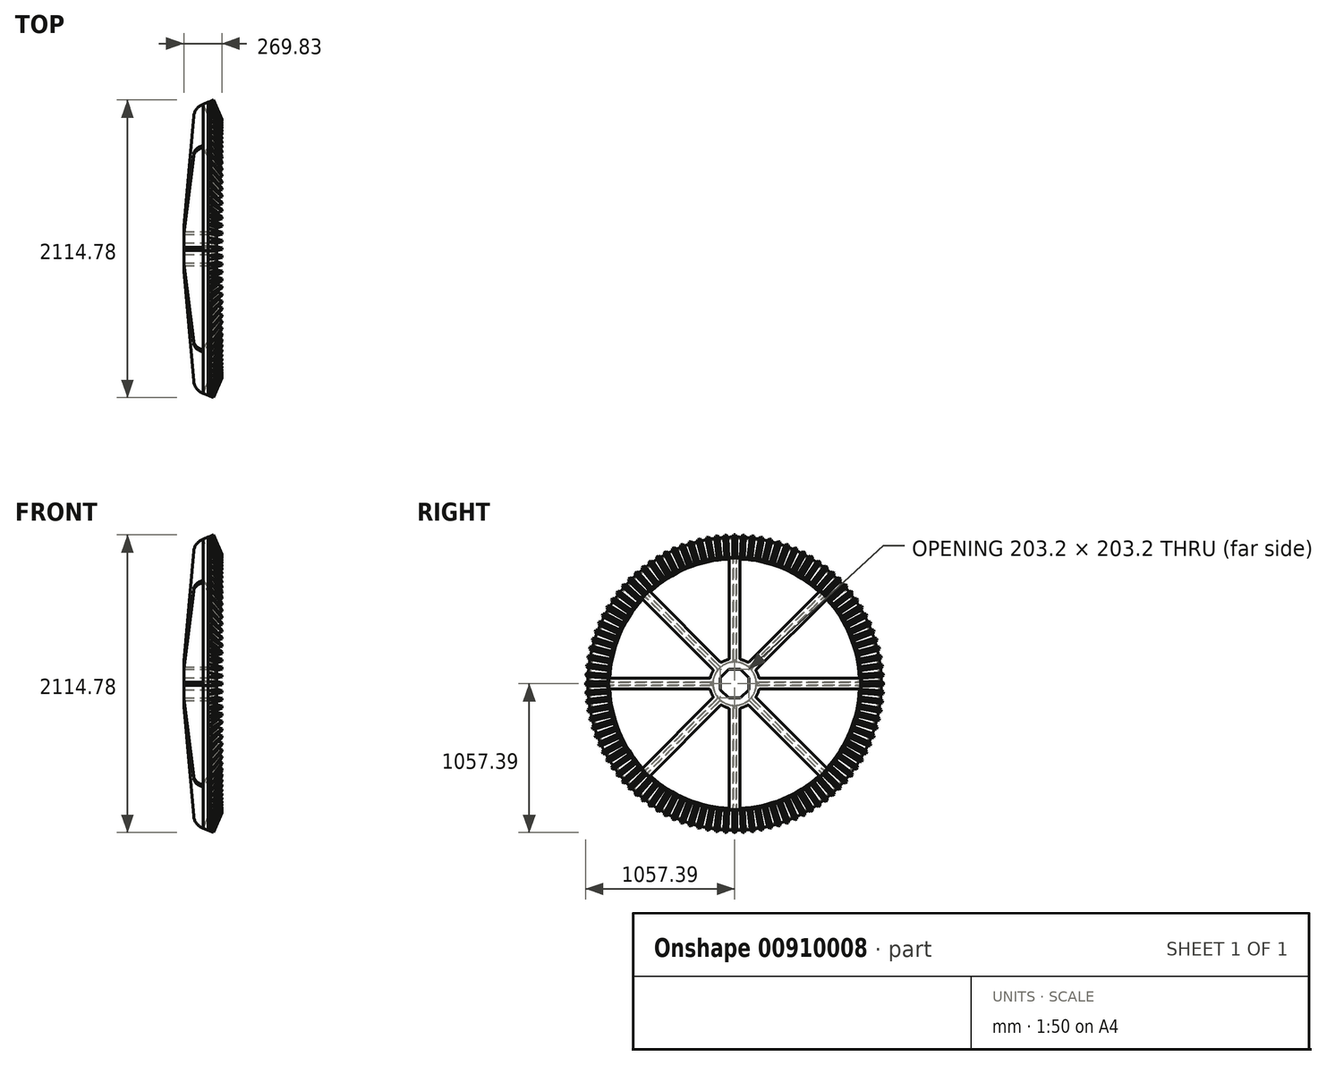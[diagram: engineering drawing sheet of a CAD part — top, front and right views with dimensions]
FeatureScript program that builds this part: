
annotation { "Feature Type Name" : "Feature", "Feature Type Description" : "" }
export const myFeature = defineFeature(function(context is Context, id is Id, definition is map)
    precondition{}
    {
        {
            var Q0;
            Q0=qCreatedBy(makeId("Front.planeOp"),FACE);
            var sketch = newSketch(context, id + "F0", { "sketchPlane" : qUnion([Q0])});
            skLineSegment(sketch, "E0.bottom", {"start": v(0, 0) * mm, "end": v(-215.9, 0) * mm});
            skLineSegment(sketch, "E0.top", {"start": v(-19.05, 154.2) * mm, "end": v(-215.9, 154.2) * mm});
            skLineSegment(sketch, "E0.right", {"start": v(-215.9, 0) * mm, "end": v(-215.9, 154.2) * mm});
            skLineSegment(sketch, "E1", {"start": v(-43.01, 1041.4) * mm, "end": v(16.07, 900.92) * mm});
            skLineSegment(sketch, "E2", {"start": v(16.07, 900.92) * mm, "end": v(-19.05, 886.15) * mm});
            skLineSegment(sketch, "E3", {"start": v(-19.05, 886.15) * mm, "end": v(-78.13, 1026.63) * mm});
            skLineSegment(sketch, "E4", {"start": v(-78.13, 1026.63) * mm, "end": v(-43.01, 1041.4) * mm});
            skLineSegment(sketch, "E5", {"start": v(-19.05, 154.2) * mm, "end": v(-19.05, 177.8) * mm});
            skLineSegment(sketch, "E6", {"start": v(-19.05, 177.8) * mm, "end": v(0, 177.8) * mm});
            skLineSegment(sketch, "E7", {"start": v(0, 177.8) * mm, "end": v(0, 0) * mm});
            skLineSegment(sketch, "E8", {"start": v(-13.47, 971.16) * mm, "end": v(-48.6, 956.39) * mm, "construction": true});
            skLineSegment(sketch, "E9", {"start": v(0, 0) * mm, "end": v(215.9, 0) * mm, "construction": true});
            skSolve(sketch);
        }
        {
            var Q0;
            Q0=makeQuery(id+"F0.imprint","IMPRINT",FACE,{"disambiguationData":[TD([[makeQuery(id+"F0.imprint","IMPRINT",EDGE,{"derivedFrom":sQuery(id+"F0.wireOp",EDGE,"E0.bottom")}),-1.0]])]});
            var Q1;
            Q1=sQuery(id+"F0.wireOp",EDGE,"E0.bottom");
            revolve(context, id + "F1", {"surfaceOperationType" : NewSurfaceOperationType.NEW, "entities" : qUnion([Q0]), "axis" : qUnion([Q1]), "revolveType" : RevolveType.SYMMETRIC, "angle" : 45 * degree});
        }
        {
            var Q0;
            Q0=qCreatedBy(makeId("Front.planeOp"),FACE);
            var sketch = newSketch(context, id + "F2", { "sketchPlane" : qUnion([Q0])});
            skLineSegment(sketch, "E10.bottom", {"start": v(0, 154.2) * mm, "end": v(-19.05, 154.2) * mm});
            skLineSegment(sketch, "E10.top", {"start": v(0, 894.16) * mm, "end": v(-19.05, 886.15) * mm});
            skLineSegment(sketch, "E10.left", {"start": v(0, 154.2) * mm, "end": v(0, 894.16) * mm});
            skLineSegment(sketch, "E10.right", {"start": v(-19.05, 154.2) * mm, "end": v(-19.05, 886.15) * mm});
            skLineSegment(sketch, "E11", {"start": v(-19.05, 886.15) * mm, "end": v(-78.13, 1026.63) * mm});
            skLineSegment(sketch, "E12", {"start": v(-78.13, 1026.63) * mm, "end": v(-83.99, 1024.17) * mm});
            skLineSegment(sketch, "E13", {"start": v(-145.8, 939.53) * mm, "end": v(-215.9, 152.4) * mm});
            skLineSegment(sketch, "E14", {"start": v(-215.9, 0) * mm, "end": v(-19.05, 0) * mm});
            skLineSegment(sketch, "E15", {"start": v(-19.05, 0) * mm, "end": v(-19.05, 154.2) * mm});
            skPoint(sketch, "E16.visualSharp", {"position": v(-140.37, 1000.45) * mm});
            skArc(sketch, "E16.filletArc", {"start": v(-83.99, 1024.17) * mm, "mid": v(-126.65, 990.43) * mm, "end": v(-145.8, 939.53) * mm});
            skLineSegment(sketch, "E17", {"start": v(-215.9, 152.4) * mm, "end": v(-215.9, 0) * mm});
            skSolve(sketch);
        }
        {
            var Q0;
            Q0=makeQuery(id+"F2.imprint","IMPRINT",FACE,{"disambiguationData":[TD([[makeQuery(id+"F2.imprint","IMPRINT",EDGE,{"derivedFrom":sQuery(id+"F2.wireOp",EDGE,"E10.bottom")}),-1.0]])]});
            extrude(context, id + "F3", {"entities" : qUnion([Q0]), "operationType" : NewBodyOperationType.ADD, "depth" : 76.2 * mm, "offsetDistance" : 25 * mm, "symmetric" : true});
        }
        {
            var Q0;
            Q0=makeQuery(id+"F2.imprint","IMPRINT",FACE,{"disambiguationData":[TD([[makeQuery(id+"F2.imprint","IMPRINT",EDGE,{"derivedFrom":sQuery(id+"F2.wireOp",EDGE,"E10.right")}),1.0]])]});
            extrude(context, id + "F4", {"entities" : qUnion([Q0]), "operationType" : NewBodyOperationType.ADD, "depth" : 22.23 * mm, "offsetDistance" : 25 * mm, "symmetric" : true});
        }
        {
            var Q0;
            Q0=makeQuery(id+"F0.imprint","IMPRINT",FACE,{"disambiguationData":[TD([[makeQuery(id+"F0.imprint","IMPRINT",EDGE,{"derivedFrom":sQuery(id+"F0.wireOp",EDGE,"E1")}),-1.0]])]});
            var Q1;
            Q1=sQuery(id+"F0.wireOp",EDGE,"E0.bottom");
            revolve(context, id + "F5", {"operationType" : NewBodyOperationType.ADD, "surfaceOperationType" : NewSurfaceOperationType.NEW, "entities" : qUnion([Q0]), "axis" : qUnion([Q1]), "revolveType" : RevolveType.SYMMETRIC, "angle" : 45 * degree});
        }
        {
            var Q0;
            Q0=makeQuery(id+"F4.boolean.opBoolean","INTERSECT",EDGE,{"derivedFrom":[makeQuery(id+"F1.opRevolve","SWEPT_FACE",FACE,{"disambiguationData":[OSD([sQuery(id+"F0.wireOp",EDGE,"E0.top")])]}),makeQuery(id+"F4.opExtrude","CAP_FACE",FACE,{"disambiguationData":[OSD([sQuery(id+"F2.wireOp",EDGE,"E10.right"),sQuery(id+"F2.wireOp",EDGE,"E11"),sQuery(id+"F2.wireOp",EDGE,"E12"),sQuery(id+"F2.wireOp",EDGE,"PsCl8xdc-vel7-nRXP-WIJk-A4uk1FeWP0Ge"),sQuery(id+"F2.wireOp",EDGE,"E13"),sQuery(id+"F2.wireOp",EDGE,"E14"),sQuery(id+"F2.wireOp",EDGE,"E15")])],"isStart":false})]});
            var Q1;
            {var subQ0=sQuery(id+"F0.wireOp",EDGE,"E5");var subQ2=sQuery(id+"F0.wireOp",EDGE,"E0.top");Q1=makeQuery(id+"F4.boolean.opBoolean","SPLIT",EDGE,{"disambiguationData":[TD([makeQuery(id+"F1.opRevolve","CAP_FACE",FACE,{"disambiguationData":[OSD([sQuery(id+"F0.wireOp",EDGE,"E0.bottom"),subQ2,sQuery(id+"F0.wireOp",EDGE,"E0.right"),subQ0,sQuery(id+"F0.wireOp",EDGE,"E6"),sQuery(id+"F0.wireOp",EDGE,"E7")])],"isStart":false})])],"derivedFrom":makeQuery(id+"F1.opRevolve","SWEPT_EDGE",EDGE,{"disambiguationData":[OSD([subQ2,subQ0])]})});}
            var Q2;
            Q2=makeQuery(id+"F4.opExtrude","CAP_EDGE",EDGE,{"disambiguationData":[OSD([sQuery(id+"F2.wireOp",EDGE,"E10.right"),sQuery(id+"F2.wireOp",EDGE,"E15")])],"isStart":false});
            var Q3;
            Q3=makeQuery(id+"F3.boolean.opBoolean","INTERSECT",EDGE,{"derivedFrom":[makeQuery(id+"F1.opRevolve","SWEPT_FACE",FACE,{"disambiguationData":[OSD([sQuery(id+"F0.wireOp",EDGE,"E6")])]}),makeQuery(id+"F3.opExtrude","CAP_FACE",FACE,{"disambiguationData":[OSD([sQuery(id+"F2.wireOp",EDGE,"E10.bottom"),sQuery(id+"F2.wireOp",EDGE,"E10.top"),sQuery(id+"F2.wireOp",EDGE,"E10.left"),sQuery(id+"F2.wireOp",EDGE,"E10.right")])],"isStart":false})]});
            var Q4;
            Q4=makeQuery(id+"F4.boolean.opBoolean","INTERSECT",EDGE,{"derivedFrom":[makeQuery(id+"F1.opRevolve","SWEPT_FACE",FACE,{"disambiguationData":[OSD([sQuery(id+"F0.wireOp",EDGE,"E0.top")])]}),makeQuery(id+"F4.opExtrude","CAP_FACE",FACE,{"disambiguationData":[OSD([sQuery(id+"F2.wireOp",EDGE,"E10.right"),sQuery(id+"F2.wireOp",EDGE,"E11"),sQuery(id+"F2.wireOp",EDGE,"E12"),sQuery(id+"F2.wireOp",EDGE,"PsCl8xdc-vel7-nRXP-WIJk-A4uk1FeWP0Ge"),sQuery(id+"F2.wireOp",EDGE,"E13"),sQuery(id+"F2.wireOp",EDGE,"E14"),sQuery(id+"F2.wireOp",EDGE,"E15")])],"isStart":true})]});
            var Q5;
            {var subQ0=sQuery(id+"F0.wireOp",EDGE,"E5");var subQ2=sQuery(id+"F0.wireOp",EDGE,"E0.top");Q5=makeQuery(id+"F4.boolean.opBoolean","SPLIT",EDGE,{"disambiguationData":[TD([makeQuery(id+"F1.opRevolve","CAP_FACE",FACE,{"disambiguationData":[OSD([sQuery(id+"F0.wireOp",EDGE,"E0.bottom"),subQ2,sQuery(id+"F0.wireOp",EDGE,"E0.right"),subQ0,sQuery(id+"F0.wireOp",EDGE,"E6"),sQuery(id+"F0.wireOp",EDGE,"E7")])],"isStart":true})])],"derivedFrom":makeQuery(id+"F1.opRevolve","SWEPT_EDGE",EDGE,{"disambiguationData":[OSD([subQ2,subQ0])]})});}
            var Q6;
            Q6=makeQuery(id+"F4.opExtrude","CAP_EDGE",EDGE,{"disambiguationData":[OSD([sQuery(id+"F2.wireOp",EDGE,"E10.right"),sQuery(id+"F2.wireOp",EDGE,"E15")])],"isStart":true});
            var Q7;
            Q7=makeQuery(id+"F3.boolean.opBoolean","INTERSECT",EDGE,{"derivedFrom":[makeQuery(id+"F1.opRevolve","SWEPT_FACE",FACE,{"disambiguationData":[OSD([sQuery(id+"F0.wireOp",EDGE,"E6")])]}),makeQuery(id+"F3.opExtrude","CAP_FACE",FACE,{"disambiguationData":[OSD([sQuery(id+"F2.wireOp",EDGE,"E10.bottom"),sQuery(id+"F2.wireOp",EDGE,"E10.top"),sQuery(id+"F2.wireOp",EDGE,"E10.left"),sQuery(id+"F2.wireOp",EDGE,"E10.right")])],"isStart":true})]});
            var Q8;
            Q8=makeQuery(id+"F5.boolean.opBoolean","INTERSECT",EDGE,{"derivedFrom":[makeQuery(id+"F4.opExtrude","CAP_FACE",FACE,{"disambiguationData":[OSD([sQuery(id+"F2.wireOp",EDGE,"E10.right"),sQuery(id+"F2.wireOp",EDGE,"E11"),sQuery(id+"F2.wireOp",EDGE,"E12"),sQuery(id+"F2.wireOp",EDGE,"PsCl8xdc-vel7-nRXP-WIJk-A4uk1FeWP0Ge"),sQuery(id+"F2.wireOp",EDGE,"E13"),sQuery(id+"F2.wireOp",EDGE,"E14"),sQuery(id+"F2.wireOp",EDGE,"E15")])],"isStart":false}),makeQuery(id+"F5.opRevolve","SWEPT_FACE",FACE,{"disambiguationData":[OSD([sQuery(id+"F0.wireOp",EDGE,"E3")])]})]});
            var Q9;
            {var subQ0=sQuery(id+"F2.wireOp",EDGE,"E10.right");var subQ1=sQuery(id+"F2.wireOp",EDGE,"E10.top");var subQ4=sQuery(id+"F0.wireOp",EDGE,"E5");Q9=makeQuery(id+"F5.boolean.opBoolean","INTERSECT",EDGE,{"derivedFrom":[makeQuery(id+"F4.boolean.opBoolean","SPLIT",FACE,{"disambiguationData":[TD([makeQuery(id+"F3.opExtrude","CAP_FACE",FACE,{"disambiguationData":[OSD([sQuery(id+"F2.wireOp",EDGE,"E10.bottom"),subQ1,sQuery(id+"F2.wireOp",EDGE,"E10.left"),subQ0])],"isStart":false})])],"derivedFrom":makeQuery(id+"F3.boolean.opBoolean","MERGE",FACE,{"derivedFrom":[makeQuery(id+"F1.opRevolve","SWEPT_FACE",FACE,{"disambiguationData":[OSD([subQ4])]}),makeQuery(id+"F3.opExtrude","SWEPT_FACE",FACE,{"disambiguationData":[OSD([subQ0])]})]})}),makeQuery(id+"F5.opRevolve","SWEPT_FACE",FACE,{"disambiguationData":[OSD([sQuery(id+"F0.wireOp",EDGE,"E3")])]})]});}
            var Q10;
            Q10=makeQuery(id+"F5.boolean.opBoolean","INTERSECT",EDGE,{"derivedFrom":[makeQuery(id+"F3.opExtrude","CAP_FACE",FACE,{"disambiguationData":[OSD([sQuery(id+"F2.wireOp",EDGE,"E10.bottom"),sQuery(id+"F2.wireOp",EDGE,"E10.top"),sQuery(id+"F2.wireOp",EDGE,"E10.left"),sQuery(id+"F2.wireOp",EDGE,"E10.right")])],"isStart":false}),makeQuery(id+"F5.opRevolve","SWEPT_FACE",FACE,{"disambiguationData":[OSD([sQuery(id+"F0.wireOp",EDGE,"E3")])]})]});
            var Q11;
            Q11=makeQuery(id+"F5.boolean.opBoolean","INTERSECT",EDGE,{"derivedFrom":[makeQuery(id+"F3.opExtrude","CAP_FACE",FACE,{"disambiguationData":[OSD([sQuery(id+"F2.wireOp",EDGE,"E10.bottom"),sQuery(id+"F2.wireOp",EDGE,"E10.top"),sQuery(id+"F2.wireOp",EDGE,"E10.left"),sQuery(id+"F2.wireOp",EDGE,"E10.right")])],"isStart":true}),makeQuery(id+"F5.opRevolve","SWEPT_FACE",FACE,{"disambiguationData":[OSD([sQuery(id+"F0.wireOp",EDGE,"E3")])]})]});
            var Q12;
            {var subQ0=sQuery(id+"F2.wireOp",EDGE,"E10.right");var subQ1=sQuery(id+"F2.wireOp",EDGE,"E10.top");var subQ4=sQuery(id+"F0.wireOp",EDGE,"E5");Q12=makeQuery(id+"F5.boolean.opBoolean","INTERSECT",EDGE,{"derivedFrom":[makeQuery(id+"F4.boolean.opBoolean","SPLIT",FACE,{"disambiguationData":[TD([makeQuery(id+"F3.opExtrude","CAP_FACE",FACE,{"disambiguationData":[OSD([sQuery(id+"F2.wireOp",EDGE,"E10.bottom"),subQ1,sQuery(id+"F2.wireOp",EDGE,"E10.left"),subQ0])],"isStart":true})])],"derivedFrom":makeQuery(id+"F3.boolean.opBoolean","MERGE",FACE,{"derivedFrom":[makeQuery(id+"F1.opRevolve","SWEPT_FACE",FACE,{"disambiguationData":[OSD([subQ4])]}),makeQuery(id+"F3.opExtrude","SWEPT_FACE",FACE,{"disambiguationData":[OSD([subQ0])]})]})}),makeQuery(id+"F5.opRevolve","SWEPT_FACE",FACE,{"disambiguationData":[OSD([sQuery(id+"F0.wireOp",EDGE,"E3")])]})]});}
            var Q13;
            Q13=makeQuery(id+"F5.boolean.opBoolean","INTERSECT",EDGE,{"derivedFrom":[makeQuery(id+"F4.opExtrude","CAP_FACE",FACE,{"disambiguationData":[OSD([sQuery(id+"F2.wireOp",EDGE,"E10.right"),sQuery(id+"F2.wireOp",EDGE,"E11"),sQuery(id+"F2.wireOp",EDGE,"E12"),sQuery(id+"F2.wireOp",EDGE,"PsCl8xdc-vel7-nRXP-WIJk-A4uk1FeWP0Ge"),sQuery(id+"F2.wireOp",EDGE,"E13"),sQuery(id+"F2.wireOp",EDGE,"E14"),sQuery(id+"F2.wireOp",EDGE,"E15")])],"isStart":true}),makeQuery(id+"F5.opRevolve","SWEPT_FACE",FACE,{"disambiguationData":[OSD([sQuery(id+"F0.wireOp",EDGE,"E3")])]})]});
            fillet(context, id + "F6", {"entities" : qUnion([Q0, Q1, Q2, Q3, Q4, Q5, Q6, Q7, Q8, Q9, Q10, Q11, Q12, Q13]), "radius" : 9.53 * mm, "tangentPropagation" : true, "allowEdgeOverflow" : false});
        }
        {
            var Q0;
            Q0=makeQuery(id+"F1.opRevolve","SWEPT_BODY",BODY,{"disambiguationData":[OSD([sQuery(id+"F0.wireOp",EDGE,"E0.bottom"),sQuery(id+"F0.wireOp",EDGE,"E0.top"),sQuery(id+"F0.wireOp",EDGE,"E0.left"),sQuery(id+"F0.wireOp",EDGE,"E0.right")])]});
            var Q1;
            Q1=makeQuery(id+"F1.opRevolve","SWEPT_BODY",BODY,{"disambiguationData":[OSD([sQuery(id+"F0.wireOp",EDGE,"E1"),sQuery(id+"F0.wireOp",EDGE,"E2"),sQuery(id+"F0.wireOp",EDGE,"E3"),sQuery(id+"F0.wireOp",EDGE,"E4")])]});
            var Q2;
            Q2=sQuery(id+"F0.wireOp",EDGE,"E0.bottom");
            circularPattern(context, id + "F7", {"operationType" : NewBodyOperationType.ADD, "entities" : qUnion([Q0, Q1]), "axis" : qUnion([Q2]), "angle" : 360 * degree, "instanceCount" : 8, "equalSpace" : true});
        }
        {
            var Q0;
            Q0=makeQuery(id+"F4.opExtrude","SWEPT_FACE",FACE,{"disambiguationData":[OSD([sQuery(id+"F2.wireOp",EDGE,"E12")])]});
            var sketch = newSketch(context, id + "F8", { "sketchPlane" : qUnion([Q0])});
            skLineSegment(sketch, "E18", {"start": v(364.04, 14.29) * mm, "end": v(364.04, -14.29) * mm});
            skLineSegment(sketch, "E19", {"start": v(364.04, -14.29) * mm, "end": v(377.07, -13.15) * mm});
            skLineSegment(sketch, "E20", {"start": v(377.07, -13.15) * mm, "end": v(405.32, -7.14) * mm});
            skLineSegment(sketch, "E21", {"start": v(405.32, -7.14) * mm, "end": v(405.32, 7.14) * mm});
            skLineSegment(sketch, "E22", {"start": v(405.32, 7.14) * mm, "end": v(377.07, 13.15) * mm});
            skLineSegment(sketch, "E23", {"start": v(377.07, 13.15) * mm, "end": v(364.04, 14.29) * mm});
            skSolve(sketch);
        }
        {
            var Q0;
            Q0=makeQuery(id+"F8.imprint","IMPRINT",FACE,{"disambiguationData":[TD([[makeQuery(id+"F8.imprint","IMPRINT",EDGE,{"derivedFrom":sQuery(id+"F8.wireOp",EDGE,"E18")}),1.0]])]});
            extrude(context, id + "F9", {"entities" : qUnion([Q0]), "oppositeDirection" : true, "depth" : 152 * mm, "offsetDistance" : 25 * mm});
        }
        {
            var Q0;
            Q0=makeQuery(id+"F9.opExtrude","SWEPT_BODY",BODY,{"disambiguationData":[OSD([sQuery(id+"F8.wireOp",EDGE,"E18"),sQuery(id+"F8.wireOp",EDGE,"E19"),sQuery(id+"F8.wireOp",EDGE,"E20"),sQuery(id+"F8.wireOp",EDGE,"E21"),sQuery(id+"F8.wireOp",EDGE,"E22"),sQuery(id+"F8.wireOp",EDGE,"E23")])]});
            var Q1;
            Q1=sQuery(id+"F0.wireOp",EDGE,"E0.bottom");
            circularPattern(context, id + "F10", {"operationType" : NewBodyOperationType.ADD, "entities" : qUnion([Q0]), "axis" : qUnion([Q1]), "angle" : 360 * degree, "instanceCount" : 104, "equalSpace" : true});
        }
        {
            var Q0;
            {var subQ0=makeQuery(id+"F3.boolean.opBoolean","MERGE",FACE,{"derivedFrom":[makeQuery(id+"F1.opRevolve","SWEPT_FACE",FACE,{"disambiguationData":[OSD([sQuery(id+"F0.wireOp",EDGE,"E7")])]}),makeQuery(id+"F3.opExtrude","SWEPT_FACE",FACE,{"disambiguationData":[OSD([sQuery(id+"F2.wireOp",EDGE,"E10.left")])]})]});Q0=makeQuery(id+"F7.boolean.opBoolean","MERGE",FACE,{"derivedFrom":[subQ0,makeQuery(id+"F7.opPattern","COPY",FACE,{"derivedFrom":subQ0,"instanceName":"1"}),makeQuery(id+"F7.opPattern","COPY",FACE,{"derivedFrom":subQ0,"instanceName":"2"}),makeQuery(id+"F7.opPattern","COPY",FACE,{"derivedFrom":subQ0,"instanceName":"3"}),makeQuery(id+"F7.opPattern","COPY",FACE,{"derivedFrom":subQ0,"instanceName":"4"}),makeQuery(id+"F7.opPattern","COPY",FACE,{"derivedFrom":subQ0,"instanceName":"5"}),makeQuery(id+"F7.opPattern","COPY",FACE,{"derivedFrom":subQ0,"instanceName":"6"}),makeQuery(id+"F7.opPattern","COPY",FACE,{"derivedFrom":subQ0,"instanceName":"7"})]});}
            var sketch = newSketch(context, id + "F11", { "sketchPlane" : qUnion([Q0])});
            skCircle(sketch, "E24.cCircle", {"center": v(0, 0) * mm, "radius": 101.6 * mm, "construction": true});
            skLineSegment(sketch, "E24.0", {"start": v(42.08, 101.6) * mm, "end": v(101.6, 42.08) * mm});
            skLineSegment(sketch, "E24.1", {"start": v(101.6, 42.08) * mm, "end": v(101.6, -42.08) * mm});
            skLineSegment(sketch, "E24.2", {"start": v(101.6, -42.08) * mm, "end": v(42.08, -101.6) * mm});
            skLineSegment(sketch, "E24.3", {"start": v(42.08, -101.6) * mm, "end": v(-42.08, -101.6) * mm});
            skLineSegment(sketch, "E24.4", {"start": v(-42.08, -101.6) * mm, "end": v(-101.6, -42.08) * mm});
            skLineSegment(sketch, "E24.5", {"start": v(-101.6, -42.08) * mm, "end": v(-101.6, 42.08) * mm});
            skLineSegment(sketch, "E24.6", {"start": v(-101.6, 42.08) * mm, "end": v(-42.08, 101.6) * mm});
            skLineSegment(sketch, "E24.7", {"start": v(-42.08, 101.6) * mm, "end": v(42.08, 101.6) * mm});
            skPoint(sketch, "E24.0.midPoint", {"position": v(71.84, 71.84) * mm});
            skSolve(sketch);
        }
        {
            var Q0;
            Q0=makeQuery(id+"F11.imprint","IMPRINT",FACE,{"disambiguationData":[TD([[makeQuery(id+"F11.imprint","IMPRINT",EDGE,{"derivedFrom":sQuery(id+"F11.wireOp",EDGE,"E24.0")}),-1.0]])]});
            extrude(context, id + "F12", {"entities" : qUnion([Q0]), "operationType" : NewBodyOperationType.REMOVE, "endBound" : BoundingType.THROUGH_ALL, "oppositeDirection" : true, "depth" : 25 * mm, "offsetDistance" : 25 * mm});
        }
    });
